# Revit family: JC KONTAKTER JCK207 Armbågskontakt
name_source: partatom
category: Specialty Equipment
units: mm (PartAtom-declared; Revit-internal decimal feet)

## family parameters
Always vertical = Yes
Cut with Voids When Loaded = No
Enable Cutting in Views = Yes
Host = Wall
Maintain Annotation Orientation = No
Part Type = Normal
Room Calculation Point = No
Round Connector Dimension = Use Diameter
Shared = No

## types (1)
- Armbågskontakt JCK207
    Antal mikrobrytare = 1
    CE Dokument = https://jckontakter.se
    Core Finish = Aluminum ENAW 6060
    Default Elevation = 0 mm  [stored 0 ft]
    Description = JCK207 tillhör en serie armbågskontakter som har en plan tryckyta med fyra taktila rillor i. Rillorna fungerar som extra vägledning för personer med synnedsättning. Man kan enkelt känna sig till vart man ska trycka för att aktivera dörröppning. JCK207 är tillverkad i silvereloxerad aluminium och har mörkgrå endcaps. Den levereras med 1st mikrobrytare i IP67.
    End Cap Finish = POM Tenac C 4520
    Lid Finish = Aluminum ENAW 6060
    Längsta märkström = 1mA/4 V DC
    Manufacturer = JC Kontakter
    Microbrytare = Standard NO IP67
    Model = JCK207
    Nominell märkström = 12 V - Resistive 6A Inductive L/R 5ms 6A, 24 V - Resistive 6A Inductive L/R 5ms 5A
    Placering information = https://jckontakter.se
    Produktvikt = 0.305 kg
    Teknisk produktblad = https://jckontakter.se
    Tillvalsförteckning = https://jckontakter.se
    Tillverkarens land = Sverige
    URL = https://jckontakter.se

note: [stored X ft] marks values corroborated as IEEE doubles in the binary element streams (Revit-internal decimal feet)

## geometry (parser evidence)
native form markers: Sweep x4
no freeform markers — native parametric forms only
